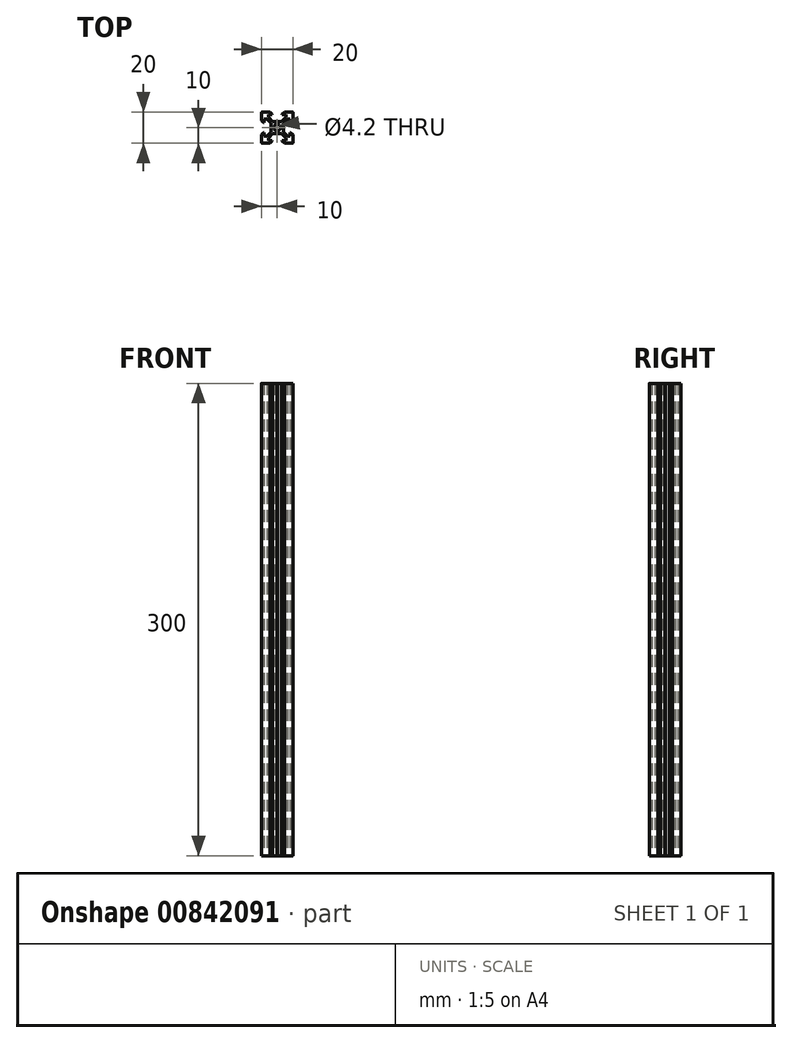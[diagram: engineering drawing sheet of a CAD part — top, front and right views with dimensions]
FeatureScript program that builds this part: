
annotation { "Feature Type Name" : "Feature", "Feature Type Description" : "" }
export const myFeature = defineFeature(function(context is Context, id is Id, definition is map)
    precondition{}
    {
        {
            var Q0;
            Q0=qCreatedBy(makeId("Top.planeOp"),FACE);
            var sketch = newSketch(context, id + "F0", { "sketchPlane" : qUnion([Q0])});
            skLineSegment(sketch, "E0.bottom", {"start": v(-9.5, 10) * mm, "end": v(-4.58, 10) * mm});
            skLineSegment(sketch, "E0.top", {"start": v(-9.5, -10) * mm, "end": v(-4.58, -10) * mm});
            skLineSegment(sketch, "E0.left", {"start": v(-10, 9.5) * mm, "end": v(-10, 4.58) * mm});
            skLineSegment(sketch, "E0.right", {"start": v(10, 9.5) * mm, "end": v(10, 4.58) * mm});
            skLineSegment(sketch, "E1", {"start": v(-10, 10) * mm, "end": v(10, -10) * mm, "construction": true});
            skLineSegment(sketch, "E2", {"start": v(-10, 0) * mm, "end": v(10, 0) * mm, "construction": true});
            skLineSegment(sketch, "E3", {"start": v(-10, 4.58) * mm, "end": v(-8.55, 3.12) * mm});
            skLineSegment(sketch, "E4", {"start": v(-8.55, 3.12) * mm, "end": v(-8.2, 3.12) * mm});
            skLineSegment(sketch, "E5", {"start": v(-8.2, 3.12) * mm, "end": v(-8.2, 5.5) * mm});
            skLineSegment(sketch, "E6", {"start": v(-8.2, 5.5) * mm, "end": v(-6.56, 5.5) * mm});
            skLineSegment(sketch, "E7", {"start": v(-6.56, 5.5) * mm, "end": v(-3.9, 2.84) * mm});
            skLineSegment(sketch, "E8", {"start": v(-3.9, 2.84) * mm, "end": v(-3.9, 0.21) * mm});
            skLineSegment(sketch, "E9", {"start": v(-3.9, 0.21) * mm, "end": v(-3.69, 0) * mm});
            skLineSegment(sketch, "E10.MirrorCS", {"start": v(-10, -4.58) * mm, "end": v(-8.55, -3.12) * mm});
            skLineSegment(sketch, "E11.MirrorCS", {"start": v(-8.55, -3.12) * mm, "end": v(-8.2, -3.12) * mm});
            skLineSegment(sketch, "E12.MirrorCS", {"start": v(-8.2, -3.12) * mm, "end": v(-8.2, -5.5) * mm});
            skLineSegment(sketch, "E13.MirrorCS", {"start": v(-8.2, -5.5) * mm, "end": v(-6.56, -5.5) * mm});
            skLineSegment(sketch, "E14.MirrorCS", {"start": v(-6.56, -5.5) * mm, "end": v(-3.9, -2.84) * mm});
            skLineSegment(sketch, "E15.MirrorCS", {"start": v(-3.9, -2.84) * mm, "end": v(-3.9, -0.21) * mm});
            skLineSegment(sketch, "E16.MirrorCS", {"start": v(-3.9, -0.2) * mm, "end": v(-3.69, 0) * mm});
            skLineSegment(sketch, "E17.MirrorCS", {"start": v(2.84, 3.9) * mm, "end": v(0.2, 3.9) * mm});
            skLineSegment(sketch, "E18.MirrorCS", {"start": v(-2.84, 3.9) * mm, "end": v(-0.21, 3.9) * mm});
            skLineSegment(sketch, "E19.MirrorCS", {"start": v(-5.5, 6.56) * mm, "end": v(-2.84, 3.9) * mm});
            skLineSegment(sketch, "E20.MirrorCS", {"start": v(-5.5, 8.2) * mm, "end": v(-5.5, 6.56) * mm});
            skLineSegment(sketch, "E21.MirrorCS", {"start": v(-3.12, 8.2) * mm, "end": v(-5.5, 8.2) * mm});
            skLineSegment(sketch, "E22.MirrorCS", {"start": v(-4.58, 10) * mm, "end": v(-3.12, 8.55) * mm});
            skLineSegment(sketch, "E23.MirrorCS", {"start": v(4.58, 10) * mm, "end": v(3.13, 8.55) * mm});
            skLineSegment(sketch, "E24.MirrorCS", {"start": v(3.13, 8.2) * mm, "end": v(5.5, 8.2) * mm});
            skLineSegment(sketch, "E25.MirrorCS", {"start": v(5.5, 8.2) * mm, "end": v(5.5, 6.56) * mm});
            skLineSegment(sketch, "E26.MirrorCS", {"start": v(5.5, 6.56) * mm, "end": v(2.84, 3.9) * mm});
            skLineSegment(sketch, "E27.MirrorCS", {"start": v(-0.21, 3.9) * mm, "end": v(0, 3.7) * mm});
            skLineSegment(sketch, "E28.MirrorCS", {"start": v(0.2, 3.9) * mm, "end": v(0, 3.7) * mm});
            skLineSegment(sketch, "E29.MirrorCS", {"start": v(-3.12, 8.55) * mm, "end": v(-3.12, 8.2) * mm});
            skLineSegment(sketch, "E30.MirrorCS", {"start": v(3.12, 8.55) * mm, "end": v(3.12, 8.2) * mm});
            skLineSegment(sketch, "E31.MirrorCS", {"start": v(-5.5, -6.56) * mm, "end": v(-2.84, -3.9) * mm});
            skLineSegment(sketch, "E32.MirrorCS", {"start": v(-5.5, -8.2) * mm, "end": v(-5.5, -6.56) * mm});
            skLineSegment(sketch, "E33.MirrorCS", {"start": v(-3.12, -8.2) * mm, "end": v(-5.5, -8.2) * mm});
            skLineSegment(sketch, "E34.MirrorCS", {"start": v(-4.58, -10) * mm, "end": v(-3.12, -8.55) * mm});
            skLineSegment(sketch, "E35.MirrorCS", {"start": v(-3.12, -8.55) * mm, "end": v(-3.12, -8.2) * mm});
            skLineSegment(sketch, "E36.MirrorCS", {"start": v(-0.21, -3.9) * mm, "end": v(0, -3.7) * mm});
            skLineSegment(sketch, "E37.MirrorCS", {"start": v(0.2, -3.9) * mm, "end": v(0, -3.7) * mm});
            skLineSegment(sketch, "E38.MirrorCS", {"start": v(-2.84, -3.9) * mm, "end": v(-0.21, -3.9) * mm});
            skLineSegment(sketch, "E39.MirrorCS", {"start": v(2.84, -3.9) * mm, "end": v(0.2, -3.9) * mm});
            skLineSegment(sketch, "E40.MirrorCS", {"start": v(5.5, -6.56) * mm, "end": v(2.84, -3.9) * mm});
            skLineSegment(sketch, "E41.MirrorCS", {"start": v(5.5, -8.2) * mm, "end": v(5.5, -6.56) * mm});
            skLineSegment(sketch, "E42.MirrorCS", {"start": v(3.13, -8.2) * mm, "end": v(5.5, -8.2) * mm});
            skLineSegment(sketch, "E43.MirrorCS", {"start": v(4.58, -10) * mm, "end": v(3.13, -8.55) * mm});
            skLineSegment(sketch, "E44.MirrorCS", {"start": v(3.12, -8.55) * mm, "end": v(3.12, -8.2) * mm});
            skLineSegment(sketch, "E45.MirrorCS", {"start": v(10, 4.58) * mm, "end": v(8.55, 3.12) * mm});
            skLineSegment(sketch, "E46.MirrorCS", {"start": v(8.2, 3.12) * mm, "end": v(8.2, 5.5) * mm});
            skLineSegment(sketch, "E47.MirrorCS", {"start": v(8.2, 5.5) * mm, "end": v(6.56, 5.5) * mm});
            skLineSegment(sketch, "E48.MirrorCS", {"start": v(6.56, 5.5) * mm, "end": v(3.9, 2.84) * mm});
            skLineSegment(sketch, "E49.MirrorCS", {"start": v(3.9, 2.84) * mm, "end": v(3.9, 0.21) * mm});
            skLineSegment(sketch, "E50.MirrorCS", {"start": v(3.9, -2.84) * mm, "end": v(3.9, -0.2) * mm});
            skLineSegment(sketch, "E51.MirrorCS", {"start": v(6.56, -5.5) * mm, "end": v(3.9, -2.84) * mm});
            skLineSegment(sketch, "E52.MirrorCS", {"start": v(8.2, -5.5) * mm, "end": v(6.56, -5.5) * mm});
            skLineSegment(sketch, "E53.MirrorCS", {"start": v(8.2, -3.13) * mm, "end": v(8.2, -5.5) * mm});
            skLineSegment(sketch, "E54.MirrorCS", {"start": v(10, -4.58) * mm, "end": v(8.55, -3.13) * mm});
            skLineSegment(sketch, "E55.MirrorCS", {"start": v(8.55, -3.12) * mm, "end": v(8.2, -3.12) * mm});
            skLineSegment(sketch, "E56.MirrorCS", {"start": v(8.55, 3.12) * mm, "end": v(8.2, 3.12) * mm});
            skLineSegment(sketch, "E57.MirrorCS", {"start": v(3.9, 0.2) * mm, "end": v(3.7, 0) * mm});
            skLineSegment(sketch, "E58.MirrorCS", {"start": v(3.9, -0.21) * mm, "end": v(3.69, 0) * mm});
            skCircle(sketch, "E59", {"center": v(0, 0) * mm, "radius": 2.1 * mm});
            skLineSegment(sketch, "E60", {"start": v(-4.58, 10) * mm, "end": v(4.58, 10) * mm, "construction": true});
            skLineSegment(sketch, "E61", {"start": v(4.58, 10) * mm, "end": v(9.5, 10) * mm});
            skLineSegment(sketch, "E62", {"start": v(10, 4.58) * mm, "end": v(10, -4.58) * mm, "construction": true});
            skLineSegment(sketch, "E63", {"start": v(10, -4.58) * mm, "end": v(10, -9.5) * mm});
            skLineSegment(sketch, "E64", {"start": v(4.58, -10) * mm, "end": v(9.5, -10) * mm});
            skLineSegment(sketch, "E65", {"start": v(-4.58, -10) * mm, "end": v(4.58, -10) * mm, "construction": true});
            skLineSegment(sketch, "E66", {"start": v(-10, -4.58) * mm, "end": v(-10, -9.5) * mm});
            skLineSegment(sketch, "E67", {"start": v(-10, 4.58) * mm, "end": v(-10, -4.58) * mm, "construction": true});
            skPoint(sketch, "E68.visualSharp", {"position": v(-10, 10) * mm});
            skArc(sketch, "E68.filletArc", {"start": v(-9.5, 10) * mm, "mid": v(-9.85, 9.85) * mm, "end": v(-10, 9.5) * mm});
            skPoint(sketch, "E69.visualSharp", {"position": v(10, 10) * mm});
            skArc(sketch, "E69.filletArc", {"start": v(10, 9.5) * mm, "mid": v(9.85, 9.85) * mm, "end": v(9.5, 10) * mm});
            skPoint(sketch, "E70.visualSharp", {"position": v(10, -10) * mm});
            skArc(sketch, "E70.filletArc", {"start": v(9.5, -10) * mm, "mid": v(9.85, -9.85) * mm, "end": v(10, -9.5) * mm});
            skPoint(sketch, "E71.visualSharp", {"position": v(-10, -10) * mm});
            skArc(sketch, "E71.filletArc", {"start": v(-10, -9.5) * mm, "mid": v(-9.85, -9.85) * mm, "end": v(-9.5, -10) * mm});
            skSolve(sketch);
        }
        {
            var Q0;
            Q0=qCreatedBy(makeId("Top.planeOp"),FACE);
            var sketch = newSketch(context, id + "F1", { "sketchPlane" : qUnion([Q0])});
            skLineSegment(sketch, "E72", {"start": v(-10, 0) * mm, "end": v(10, 0) * mm, "construction": true});
            skLineSegment(sketch, "E73", {"start": v(-10, 0) * mm, "end": v(-10, 5.42) * mm});
            skLineSegment(sketch, "E74", {"start": v(-10, 5.42) * mm, "end": v(-8.54, 6.87) * mm});
            skLineSegment(sketch, "E75", {"start": v(-8.54, 6.87) * mm, "end": v(-8.2, 6.87) * mm});
            skLineSegment(sketch, "E76", {"start": v(-8.2, 6.87) * mm, "end": v(-8.2, 4.5) * mm});
            skLineSegment(sketch, "E77", {"start": v(-8.2, 4.5) * mm, "end": v(-6.56, 4.5) * mm});
            skLineSegment(sketch, "E78", {"start": v(-6.56, 4.5) * mm, "end": v(-3.9, 7.16) * mm});
            skLineSegment(sketch, "E79", {"start": v(-3.9, 10.21) * mm, "end": v(-3.7, 10) * mm});
            skLineSegment(sketch, "E80", {"start": v(-3.69, 10) * mm, "end": v(-12.1, 10) * mm, "construction": true});
            skLineSegment(sketch, "E81.MirrorCS", {"start": v(-3.9, 9.8) * mm, "end": v(-3.69, 10) * mm});
            skLineSegment(sketch, "E82.MirrorCS", {"start": v(-6.56, 15.5) * mm, "end": v(-3.9, 12.84) * mm});
            skLineSegment(sketch, "E83.MirrorCS", {"start": v(-8.2, 15.5) * mm, "end": v(-6.56, 15.5) * mm});
            skLineSegment(sketch, "E84.MirrorCS", {"start": v(-8.2, 13.13) * mm, "end": v(-8.2, 15.5) * mm});
            skLineSegment(sketch, "E85.MirrorCS", {"start": v(-8.54, 13.12) * mm, "end": v(-8.2, 13.12) * mm});
            skLineSegment(sketch, "E86.MirrorCS", {"start": v(-10, 14.58) * mm, "end": v(-8.54, 13.13) * mm});
            skLineSegment(sketch, "E87", {"start": v(-10, 14.58) * mm, "end": v(-10, 19.5) * mm});
            skLineSegment(sketch, "E88", {"start": v(0, 0) * mm, "end": v(0, 2.38) * mm, "construction": true});
            skLineSegment(sketch, "E89", {"start": v(-3.9, 7.16) * mm, "end": v(-3.9, 9.8) * mm});
            skLineSegment(sketch, "E90", {"start": v(-3.9, 10.21) * mm, "end": v(-3.9, 12.84) * mm});
            skLineSegment(sketch, "E91", {"start": v(-10, 0) * mm, "end": v(-8.64, 1.36) * mm, "construction": true});
            skLineSegment(sketch, "E92", {"start": v(-7.19, 17.19) * mm, "end": v(-4.36, 14.36) * mm, "construction": true});
            skLineSegment(sketch, "E93.MirrorCS", {"start": v(-4.58, 20) * mm, "end": v(-9.5, 20) * mm});
            skLineSegment(sketch, "E94.MirrorCS", {"start": v(-4.58, 20) * mm, "end": v(-3.13, 18.54) * mm});
            skLineSegment(sketch, "E95.MirrorCS", {"start": v(-3.13, 18.54) * mm, "end": v(-3.13, 18.2) * mm});
            skLineSegment(sketch, "E96.MirrorCS", {"start": v(-3.13, 18.2) * mm, "end": v(-5.5, 18.2) * mm});
            skLineSegment(sketch, "E97.MirrorCS", {"start": v(-5.5, 18.2) * mm, "end": v(-5.5, 16.56) * mm});
            skLineSegment(sketch, "E98.MirrorCS", {"start": v(-5.5, 16.56) * mm, "end": v(-2.84, 13.9) * mm});
            skArc(sketch, "E99.filletArc", {"start": v(-9.5, 20) * mm, "mid": v(-9.85, 19.85) * mm, "end": v(-10, 19.5) * mm});
            skLineSegment(sketch, "E100.MirrorCS", {"start": v(-6.24, 2.7) * mm, "end": v(-2.84, 6.1) * mm});
            skLineSegment(sketch, "E101.MirrorCS", {"start": v(3.9, 10.21) * mm, "end": v(3.9, 12.84) * mm});
            skLineSegment(sketch, "E102.MirrorCS", {"start": v(3.9, 7.16) * mm, "end": v(3.9, 9.8) * mm});
            skLineSegment(sketch, "E103.MirrorCS", {"start": v(3.9, 9.8) * mm, "end": v(3.69, 10) * mm});
            skLineSegment(sketch, "E104.MirrorCS", {"start": v(3.9, 10.21) * mm, "end": v(3.69, 10) * mm});
            skLineSegment(sketch, "E105.MirrorCS", {"start": v(6.56, 15.5) * mm, "end": v(3.9, 12.84) * mm});
            skLineSegment(sketch, "E106.MirrorCS", {"start": v(6.56, 4.5) * mm, "end": v(3.9, 7.16) * mm});
            skLineSegment(sketch, "E107.MirrorCS", {"start": v(8.2, 4.5) * mm, "end": v(6.56, 4.5) * mm});
            skLineSegment(sketch, "E108.MirrorCS", {"start": v(8.2, 6.87) * mm, "end": v(8.2, 4.5) * mm});
            skLineSegment(sketch, "E109.MirrorCS", {"start": v(8.54, 6.88) * mm, "end": v(8.2, 6.88) * mm});
            skLineSegment(sketch, "E110.MirrorCS", {"start": v(10, 5.42) * mm, "end": v(8.54, 6.87) * mm});
            skLineSegment(sketch, "E111.MirrorCS", {"start": v(8.54, 13.13) * mm, "end": v(8.2, 13.13) * mm});
            skLineSegment(sketch, "E112.MirrorCS", {"start": v(8.2, 15.5) * mm, "end": v(6.56, 15.5) * mm});
            skLineSegment(sketch, "E113.MirrorCS", {"start": v(8.2, 13.13) * mm, "end": v(8.2, 15.5) * mm});
            skLineSegment(sketch, "E114.MirrorCS", {"start": v(10, 14.58) * mm, "end": v(8.55, 13.12) * mm});
            skLineSegment(sketch, "E115.MirrorCS", {"start": v(10, 14.58) * mm, "end": v(10, 19.5) * mm});
            skLineSegment(sketch, "E116.MirrorCS", {"start": v(4.58, 20) * mm, "end": v(9.5, 20) * mm});
            skArc(sketch, "E117.MirrorCS", {"start": v(9.5, 20) * mm, "mid": v(9.85, 19.85) * mm, "end": v(10, 19.5) * mm});
            skLineSegment(sketch, "E118.MirrorCS", {"start": v(3.12, 18.54) * mm, "end": v(3.12, 18.2) * mm});
            skLineSegment(sketch, "E119.MirrorCS", {"start": v(5.5, 18.2) * mm, "end": v(5.5, 16.56) * mm});
            skLineSegment(sketch, "E120.MirrorCS", {"start": v(3.13, 18.2) * mm, "end": v(5.5, 18.2) * mm});
            skLineSegment(sketch, "E121.MirrorCS", {"start": v(5.5, 16.56) * mm, "end": v(2.84, 13.9) * mm});
            skLineSegment(sketch, "E122.MirrorCS", {"start": v(4.58, 20) * mm, "end": v(3.12, 18.54) * mm});
            skLineSegment(sketch, "E123.MirrorCS", {"start": v(10, 0) * mm, "end": v(10, 5.42) * mm});
            skLineSegment(sketch, "E124.MirrorCS", {"start": v(-0.21, 13.9) * mm, "end": v(-2.84, 13.9) * mm});
            skLineSegment(sketch, "E125.MirrorCS", {"start": v(2.84, 13.9) * mm, "end": v(0.2, 13.9) * mm});
            skLineSegment(sketch, "E126.MirrorCS", {"start": v(-0.2, 13.9) * mm, "end": v(0, 13.7) * mm});
            skLineSegment(sketch, "E127.MirrorCS", {"start": v(0.2, 13.9) * mm, "end": v(0, 13.7) * mm});
            skLineSegment(sketch, "E128", {"start": v(-6.24, 2.7) * mm, "end": v(-8.2, 2.7) * mm});
            skLineSegment(sketch, "E129", {"start": v(-8.2, 2.7) * mm, "end": v(-8.2, 0) * mm});
            skLineSegment(sketch, "E130.MirrorCS", {"start": v(8.2, 2.7) * mm, "end": v(8.2, 0) * mm});
            skLineSegment(sketch, "E131.MirrorCS", {"start": v(6.24, 2.7) * mm, "end": v(8.2, 2.7) * mm});
            skLineSegment(sketch, "E132.MirrorCS", {"start": v(6.24, 2.7) * mm, "end": v(2.84, 6.1) * mm});
            skLineSegment(sketch, "E133", {"start": v(-2.84, 13.9) * mm, "end": v(-3.9, 12.84) * mm, "construction": true});
            skLineSegment(sketch, "E134", {"start": v(-2.84, 6.1) * mm, "end": v(-3.9, 7.16) * mm, "construction": true});
            skCircle(sketch, "E135", {"center": v(0, 10) * mm, "radius": 2.1 * mm});
            skLineSegment(sketch, "E136.MirrorCS", {"start": v(-3.9, -9.8) * mm, "end": v(-3.69, -10) * mm});
            skLineSegment(sketch, "E137.MirrorCS", {"start": v(-3.9, -10.21) * mm, "end": v(-3.69, -10) * mm});
            skLineSegment(sketch, "E138.MirrorCS", {"start": v(3.9, -9.8) * mm, "end": v(3.69, -10) * mm});
            skLineSegment(sketch, "E139.MirrorCS", {"start": v(-8.54, -6.88) * mm, "end": v(-8.2, -6.88) * mm});
            skLineSegment(sketch, "E140.MirrorCS", {"start": v(8.54, -13.12) * mm, "end": v(8.2, -13.12) * mm});
            skLineSegment(sketch, "E141.MirrorCS", {"start": v(3.9, -10.21) * mm, "end": v(3.69, -10) * mm});
            skLineSegment(sketch, "E142.MirrorCS", {"start": v(-8.54, -13.12) * mm, "end": v(-8.2, -13.12) * mm});
            skLineSegment(sketch, "E143.MirrorCS", {"start": v(8.54, -6.88) * mm, "end": v(8.2, -6.88) * mm});
            skLineSegment(sketch, "E144.MirrorCS", {"start": v(-8.2, -13.13) * mm, "end": v(-8.2, -15.5) * mm});
            skLineSegment(sketch, "E145.MirrorCS", {"start": v(-6.24, -2.7) * mm, "end": v(-8.2, -2.7) * mm});
            skCircle(sketch, "E146.MirrorC", {"center": v(0, -10) * mm, "radius": 2.1 * mm});
            skLineSegment(sketch, "E147.MirrorCS", {"start": v(10, -14.58) * mm, "end": v(8.55, -13.12) * mm});
            skLineSegment(sketch, "E148.MirrorCS", {"start": v(6.56, -4.5) * mm, "end": v(3.9, -7.16) * mm});
            skLineSegment(sketch, "E149.MirrorCS", {"start": v(-3.9, -10.21) * mm, "end": v(-3.9, -12.84) * mm});
            skLineSegment(sketch, "E150.MirrorCS", {"start": v(6.24, -2.7) * mm, "end": v(8.2, -2.7) * mm});
            skLineSegment(sketch, "E151.MirrorCS", {"start": v(10, -5.42) * mm, "end": v(8.54, -6.87) * mm});
            skLineSegment(sketch, "E152.MirrorCS", {"start": v(8.2, -13.13) * mm, "end": v(8.2, -15.5) * mm});
            skLineSegment(sketch, "E153.MirrorCS", {"start": v(8.2, -4.5) * mm, "end": v(6.56, -4.5) * mm});
            skLineSegment(sketch, "E154.MirrorCS", {"start": v(8.2, -6.87) * mm, "end": v(8.2, -4.5) * mm});
            skLineSegment(sketch, "E155.MirrorCS", {"start": v(3.9, -10.21) * mm, "end": v(3.9, -12.84) * mm});
            skLineSegment(sketch, "E156.MirrorCS", {"start": v(6.56, -15.5) * mm, "end": v(3.9, -12.84) * mm});
            skLineSegment(sketch, "E157.MirrorCS", {"start": v(-3.9, -7.16) * mm, "end": v(-3.9, -9.8) * mm});
            skLineSegment(sketch, "E158.MirrorCS", {"start": v(-8.2, -6.87) * mm, "end": v(-8.2, -4.5) * mm});
            skLineSegment(sketch, "E159.MirrorCS", {"start": v(-10, -5.42) * mm, "end": v(-8.54, -6.87) * mm});
            skLineSegment(sketch, "E160.MirrorCS", {"start": v(-8.2, -4.5) * mm, "end": v(-6.56, -4.5) * mm});
            skLineSegment(sketch, "E161.MirrorCS", {"start": v(-8.2, -2.7) * mm, "end": v(-8.2, 0) * mm});
            skLineSegment(sketch, "E162.MirrorCS", {"start": v(3.9, -7.16) * mm, "end": v(3.9, -9.8) * mm});
            skLineSegment(sketch, "E163.MirrorCS", {"start": v(-6.56, -15.5) * mm, "end": v(-3.9, -12.84) * mm});
            skLineSegment(sketch, "E164.MirrorCS", {"start": v(-8.2, -15.5) * mm, "end": v(-6.56, -15.5) * mm});
            skLineSegment(sketch, "E165.MirrorCS", {"start": v(-10, -14.58) * mm, "end": v(-8.55, -13.12) * mm});
            skLineSegment(sketch, "E166.MirrorCS", {"start": v(8.2, -2.7) * mm, "end": v(8.2, 0) * mm});
            skLineSegment(sketch, "E167.MirrorCS", {"start": v(8.2, -15.5) * mm, "end": v(6.56, -15.5) * mm});
            skLineSegment(sketch, "E168.MirrorCS", {"start": v(-6.24, -2.7) * mm, "end": v(-2.84, -6.1) * mm});
            skLineSegment(sketch, "E169.MirrorCS", {"start": v(-6.56, -4.5) * mm, "end": v(-3.9, -7.16) * mm});
            skLineSegment(sketch, "E170.MirrorCS", {"start": v(10, 0) * mm, "end": v(10, -5.42) * mm});
            skLineSegment(sketch, "E171.MirrorCS", {"start": v(6.24, -2.7) * mm, "end": v(2.84, -6.1) * mm});
            skLineSegment(sketch, "E172.MirrorCS", {"start": v(-10, 0) * mm, "end": v(-10, -5.42) * mm});
            skLineSegment(sketch, "E173", {"start": v(-3.7, -10) * mm, "end": v(3.7, -10) * mm, "construction": true});
            skLineSegment(sketch, "E174.MirrorCS", {"start": v(-10, -20) * mm, "end": v(-10, -14.58) * mm});
            skLineSegment(sketch, "E175.MirrorCS", {"start": v(10, -20) * mm, "end": v(10, -14.58) * mm});
            skLineSegment(sketch, "E176.MirrorCS", {"start": v(8.2, -17.3) * mm, "end": v(8.2, -20) * mm});
            skLineSegment(sketch, "E177.MirrorCS", {"start": v(6.24, -17.3) * mm, "end": v(8.2, -17.3) * mm});
            skLineSegment(sketch, "E178.MirrorCS", {"start": v(6.24, -17.3) * mm, "end": v(2.84, -13.9) * mm});
            skLineSegment(sketch, "E179.MirrorCS", {"start": v(-6.24, -17.3) * mm, "end": v(-2.84, -13.9) * mm});
            skLineSegment(sketch, "E180.MirrorCS", {"start": v(-6.24, -17.3) * mm, "end": v(-8.2, -17.3) * mm});
            skLineSegment(sketch, "E181.MirrorCS", {"start": v(-8.2, -17.3) * mm, "end": v(-8.2, -20) * mm});
            skLineSegment(sketch, "E182.MirrorCS", {"start": v(-3.9, -30.21) * mm, "end": v(-3.69, -30) * mm});
            skLineSegment(sketch, "E183.MirrorCS", {"start": v(-3.9, -29.8) * mm, "end": v(-3.7, -30) * mm});
            skLineSegment(sketch, "E184.MirrorCS", {"start": v(0.2, -33.9) * mm, "end": v(0, -33.69) * mm});
            skLineSegment(sketch, "E185.MirrorCS", {"start": v(-0.2, -33.9) * mm, "end": v(0, -33.7) * mm});
            skLineSegment(sketch, "E186.MirrorCS", {"start": v(-3.13, -38.55) * mm, "end": v(-3.13, -38.2) * mm});
            skLineSegment(sketch, "E187.MirrorCS", {"start": v(8.54, -26.88) * mm, "end": v(8.2, -26.88) * mm});
            skLineSegment(sketch, "E188.MirrorCS", {"start": v(-8.54, -26.88) * mm, "end": v(-8.2, -26.88) * mm});
            skLineSegment(sketch, "E189.MirrorCS", {"start": v(3.9, -29.8) * mm, "end": v(3.69, -30) * mm});
            skLineSegment(sketch, "E190.MirrorCS", {"start": v(8.54, -33.12) * mm, "end": v(8.2, -33.12) * mm});
            skLineSegment(sketch, "E191.MirrorCS", {"start": v(3.12, -38.54) * mm, "end": v(3.12, -38.2) * mm});
            skLineSegment(sketch, "E192.MirrorCS", {"start": v(-8.54, -33.12) * mm, "end": v(-8.2, -33.12) * mm});
            skArc(sketch, "E193.MirrorCS", {"start": v(-9.5, -40) * mm, "mid": v(-9.85, -39.85) * mm, "end": v(-10, -39.5) * mm});
            skArc(sketch, "E194.MirrorCS", {"start": v(9.5, -40) * mm, "mid": v(9.85, -39.85) * mm, "end": v(10, -39.5) * mm});
            skLineSegment(sketch, "E195.MirrorCS", {"start": v(3.9, -30.21) * mm, "end": v(3.69, -30) * mm});
            skLineSegment(sketch, "E196.MirrorCS", {"start": v(-10, -34.58) * mm, "end": v(-8.54, -33.12) * mm});
            skLineSegment(sketch, "E197.MirrorCS", {"start": v(-0.21, -33.9) * mm, "end": v(-2.84, -33.9) * mm});
            skLineSegment(sketch, "E198.MirrorCS", {"start": v(-8.2, -24.5) * mm, "end": v(-6.56, -24.5) * mm});
            skLineSegment(sketch, "E199.MirrorCS", {"start": v(-6.24, -22.7) * mm, "end": v(-8.2, -22.7) * mm});
            skLineSegment(sketch, "E200.MirrorCS", {"start": v(-8.2, -33.12) * mm, "end": v(-8.2, -35.5) * mm});
            skLineSegment(sketch, "E201.MirrorCS", {"start": v(-3.9, -27.16) * mm, "end": v(-3.9, -29.8) * mm});
            skLineSegment(sketch, "E202.MirrorCS", {"start": v(5.5, -36.56) * mm, "end": v(2.84, -33.9) * mm});
            skLineSegment(sketch, "E203.MirrorCS", {"start": v(6.56, -35.5) * mm, "end": v(3.9, -32.84) * mm});
            skLineSegment(sketch, "E204.MirrorCS", {"start": v(-5.5, -38.2) * mm, "end": v(-5.5, -36.56) * mm});
            skLineSegment(sketch, "E205.MirrorCS", {"start": v(8.2, -33.12) * mm, "end": v(8.2, -35.5) * mm});
            skLineSegment(sketch, "E206.MirrorCS", {"start": v(-3.9, -30.21) * mm, "end": v(-3.9, -32.84) * mm});
            skLineSegment(sketch, "E207.MirrorCS", {"start": v(-10, -34.58) * mm, "end": v(-10, -39.5) * mm});
            skLineSegment(sketch, "E208.MirrorCS", {"start": v(-10, -25.42) * mm, "end": v(-8.54, -26.88) * mm});
            skLineSegment(sketch, "E209.MirrorCS", {"start": v(-8.2, -26.88) * mm, "end": v(-8.2, -24.5) * mm});
            skCircle(sketch, "E210.MirrorC", {"center": v(0, -30) * mm, "radius": 2.1 * mm});
            skLineSegment(sketch, "E211.MirrorCS", {"start": v(8.2, -24.5) * mm, "end": v(6.56, -24.5) * mm});
            skLineSegment(sketch, "E212.MirrorCS", {"start": v(-4.58, -40) * mm, "end": v(-9.5, -40) * mm});
            skLineSegment(sketch, "E213.MirrorCS", {"start": v(3.9, -30.21) * mm, "end": v(3.9, -32.84) * mm});
            skLineSegment(sketch, "E214.MirrorCS", {"start": v(8.2, -26.88) * mm, "end": v(8.2, -24.5) * mm});
            skLineSegment(sketch, "E215.MirrorCS", {"start": v(3.9, -27.16) * mm, "end": v(3.9, -29.8) * mm});
            skLineSegment(sketch, "E216.MirrorCS", {"start": v(6.24, -22.7) * mm, "end": v(8.2, -22.7) * mm});
            skLineSegment(sketch, "E217.MirrorCS", {"start": v(10, -25.42) * mm, "end": v(8.54, -26.88) * mm});
            skLineSegment(sketch, "E218.MirrorCS", {"start": v(2.84, -33.9) * mm, "end": v(0.2, -33.9) * mm});
            skLineSegment(sketch, "E219.MirrorCS", {"start": v(6.24, -22.7) * mm, "end": v(2.84, -26.1) * mm});
            skLineSegment(sketch, "E220.MirrorCS", {"start": v(8.2, -35.5) * mm, "end": v(6.56, -35.5) * mm});
            skLineSegment(sketch, "E221.MirrorCS", {"start": v(-3.13, -38.2) * mm, "end": v(-5.5, -38.2) * mm});
            skLineSegment(sketch, "E222.MirrorCS", {"start": v(-4.58, -40) * mm, "end": v(-3.13, -38.55) * mm});
            skLineSegment(sketch, "E223.MirrorCS", {"start": v(4.58, -40) * mm, "end": v(3.12, -38.54) * mm});
            skLineSegment(sketch, "E224.MirrorCS", {"start": v(6.56, -24.5) * mm, "end": v(3.9, -27.16) * mm});
            skLineSegment(sketch, "E225.MirrorCS", {"start": v(5.5, -38.2) * mm, "end": v(5.5, -36.56) * mm});
            skLineSegment(sketch, "E226.MirrorCS", {"start": v(-6.24, -22.7) * mm, "end": v(-2.84, -26.1) * mm});
            skLineSegment(sketch, "E227.MirrorCS", {"start": v(-6.56, -24.5) * mm, "end": v(-3.9, -27.16) * mm});
            skLineSegment(sketch, "E228.MirrorCS", {"start": v(4.58, -40) * mm, "end": v(9.5, -40) * mm});
            skLineSegment(sketch, "E229.MirrorCS", {"start": v(-6.56, -35.5) * mm, "end": v(-3.9, -32.84) * mm});
            skLineSegment(sketch, "E230.MirrorCS", {"start": v(-8.2, -35.5) * mm, "end": v(-6.56, -35.5) * mm});
            skLineSegment(sketch, "E231.MirrorCS", {"start": v(10, -34.58) * mm, "end": v(8.54, -33.12) * mm});
            skLineSegment(sketch, "E232.MirrorCS", {"start": v(-5.5, -36.56) * mm, "end": v(-2.84, -33.9) * mm});
            skLineSegment(sketch, "E233.MirrorCS", {"start": v(10, -34.58) * mm, "end": v(10, -39.5) * mm});
            skLineSegment(sketch, "E234.MirrorCS", {"start": v(3.13, -38.2) * mm, "end": v(5.5, -38.2) * mm});
            skLineSegment(sketch, "E235.MirrorCS", {"start": v(10, -20) * mm, "end": v(10, -25.42) * mm});
            skLineSegment(sketch, "E236.MirrorCS", {"start": v(8.2, -22.7) * mm, "end": v(8.2, -20) * mm});
            skLineSegment(sketch, "E237.MirrorCS", {"start": v(-10, -20) * mm, "end": v(-10, -25.42) * mm});
            skLineSegment(sketch, "E238.MirrorCS", {"start": v(-8.2, -22.7) * mm, "end": v(-8.2, -20) * mm});
            skLineSegment(sketch, "E239", {"start": v(2.84, 6.1) * mm, "end": v(-2.84, 6.1) * mm});
            skLineSegment(sketch, "E240.MirrorCS", {"start": v(2.84, -6.1) * mm, "end": v(-2.84, -6.1) * mm});
            skLineSegment(sketch, "E241.MirrorCS", {"start": v(2.84, -26.1) * mm, "end": v(-2.84, -26.1) * mm});
            skLineSegment(sketch, "E242.MirrorCS", {"start": v(2.84, -13.9) * mm, "end": v(-2.84, -13.9) * mm});
            skSolve(sketch);
        }
        {
            var Q0;
            Q0 = qSketchRegion(id + "F0", true);
            extrude(context, id + "F2", {"entities" : qUnion([Q0]), "depth" : 300 * mm, "offsetDistance" : 25 * mm});
        }
    });
